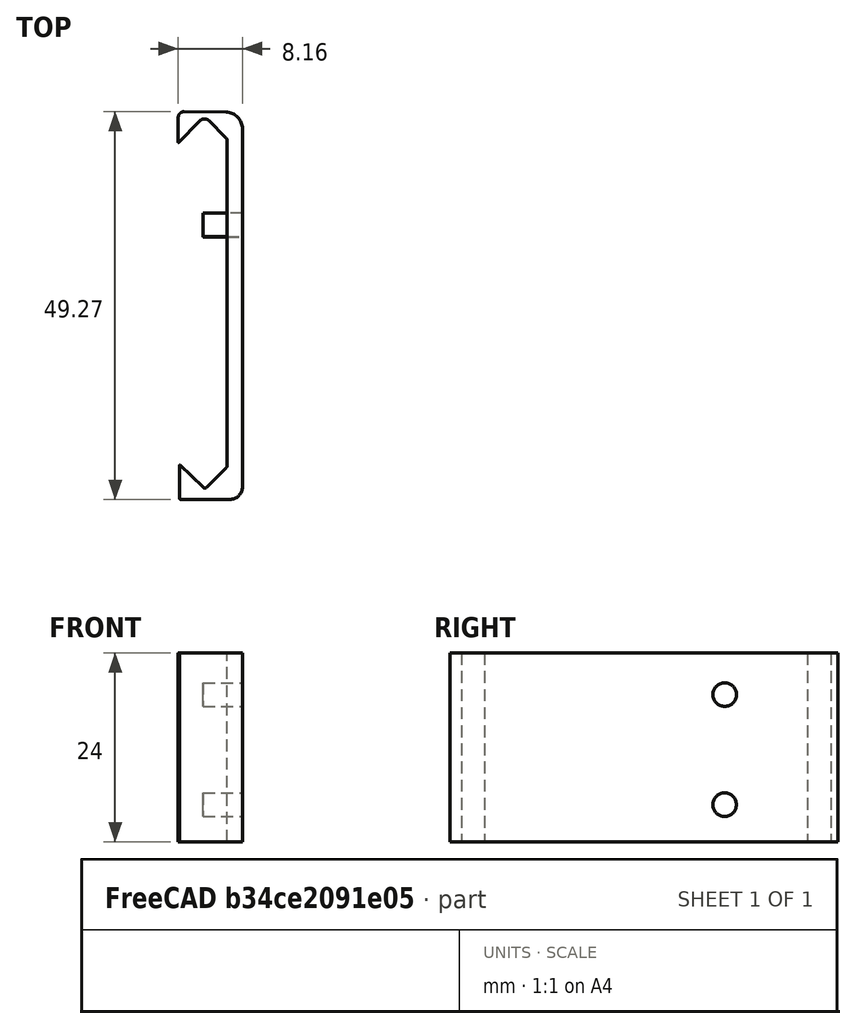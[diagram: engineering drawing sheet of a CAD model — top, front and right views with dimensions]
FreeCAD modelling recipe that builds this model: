
FCSTD DOCUMENT  (FreeCAD 0.14R2935 (Git))
Label: shapeoko-x-axis-limit-switch-mount
License: CC-BY 3.0
LicenseURL: http://creativecommons.org/licenses/by/3.0/
objects: Sketcher::SketchObject×2, PartDesign::Pad×1, PartDesign::Pocket×1
note: 6 computed .brp shape members not serialized (recipe doc carries the construction recipe); baked Part::Feature solids carry a one-line shape summary decoded from their .brp

FEATURE [Sketcher::SketchObject] Sketch002
  sketch-geometry (20):
    g0: LineSegment StartX=10.5567 StartY=23.2356 StartZ=0 EndX=12.6569 EndY=21.1244 EndZ=0
    g1: LineSegment StartX=12.8456 StartY=20.667 StartZ=0 EndX=12.8456 EndY=-20.4936 EndZ=0
    g2: LineSegment StartX=12.691 StartY=-20.8684 StartZ=0 EndX=10.2681 EndY=-23.3051 EndZ=0
    g3: LineSegment StartX=9.74691 StartY=-23.309 StartZ=0 EndX=6.87781 EndY=-20.5076 EndZ=0
    g4: LineSegment StartX=6.77176 StartY=-20.5523 StartZ=0 EndX=6.77176 EndY=-24.6612 EndZ=0
    g5: LineSegment StartX=6.97769 StartY=-24.8671 StartZ=0 EndX=13.1623 EndY=-24.8671 EndZ=0
    g6: LineSegment StartX=14.7796 StartY=-23.2498 StartZ=0 EndX=14.7796 EndY=22.2238 EndZ=0
    g7: LineSegment StartX=12.7053 StartY=24.3261 StartZ=0 EndX=7.38729 EndY=24.3974 EndZ=0
    g8: LineSegment StartX=6.61982 StartY=23.6389 StartZ=0 EndX=6.62491 EndY=20.517 EndZ=0
    g9: ArcOfCircle CenterX=7.37714 CenterY=23.6401 CenterZ=0 NormalX=0 NormalY=0 NormalZ=1 Radius=0.757326 StartAngle=1.5574 EndAngle=3.14322
    g10: ArcOfCircle CenterX=12.6771 CenterY=22.2238 CenterZ=0 NormalX=0 NormalY=0 NormalZ=1 Radius=2.10248 StartAngle=0 EndAngle=1.5574
    g11: ArcOfCircle CenterX=13.1623 CenterY=-23.2498 CenterZ=0 NormalX=0 NormalY=0 NormalZ=1 Radius=1.6173 StartAngle=4.71239 EndAngle=6.28319
    g12: ArcOfCircle CenterX=6.97769 CenterY=-24.6612 CenterZ=0 NormalX=0 NormalY=0 NormalZ=1 Radius=0.205926 StartAngle=3.14159 EndAngle=4.71239
    g13: ArcOfCircle CenterX=6.8342 CenterY=-20.5523 CenterZ=0 NormalX=0 NormalY=0 NormalZ=1 Radius=0.0624343 StartAngle=0.797343 EndAngle=3.14159
    g14: ArcOfCircle CenterX=10.0056 CenterY=-23.044 CenterZ=0 NormalX=0 NormalY=0 NormalZ=1 Radius=0.370259 StartAngle=3.93894 EndAngle=5.50063
    g15: ArcOfCircle CenterX=12.314 CenterY=-20.4936 CenterZ=0 NormalX=0 NormalY=0 NormalZ=1 Radius=0.531611 StartAngle=5.50063 EndAngle=6.28319
    g16: ArcOfCircle CenterX=12.197 CenterY=20.667 CenterZ=0 NormalX=0 NormalY=0 NormalZ=1 Radius=0.648614 StartAngle=0 EndAngle=0.78279
    g17: ArcOfCircle CenterX=9.95822 CenterY=22.6402 CenterZ=0 NormalX=0 NormalY=0 NormalZ=1 Radius=0.844143 StartAngle=0.78279 EndAngle=2.36762
    g18: LineSegment StartX=6.68048 StartY=20.4944 StartZ=0 EndX=9.35454 EndY=23.2303 EndZ=0
    g19: ArcOfCircle CenterX=6.65731 CenterY=20.5171 CenterZ=0 NormalX=0 NormalY=0 NormalZ=1 Radius=0.0323969 StartAngle=3.14322 EndAngle=5.50921
  constraints (25):
    c: Vertical(g1)
    c: Vertical(g4)
    c: Horizontal(g5)
    c: Vertical(g6)
    c: Tangent(g7,g9) = -1.5708
    c: Tangent(g8,g9) = -1.5708
    c: Tangent(g6,g10) = -1.5708
    c: Tangent(g7,g10) = -1.5708
    c: Tangent(g5,g11) = -1.5708
    c: Tangent(g6,g11) = -1.5708
    c: Tangent(g4,g12) = -1.5708
    c: Tangent(g5,g12) = -1.5708
    c: Tangent(g3,g13) = -1.5708
    c: Tangent(g4,g13) = -1.5708
    c: Tangent(g2,g14) = 1.5708
    c: Tangent(g3,g14) = 1.5708
    c: Tangent(g1,g15) = 1.5708
    c: Tangent(g2,g15) = 1.5708
    c: Tangent(g0,g16) = 1.5708
    c: Tangent(g1,g16) = 1.5708
    c: Tangent(g0,g17) = 1.5708
    c: Tangent(g18,g17)
    c: Coincident(g17,g18)
    c: Tangent(g8,g19)
    c: Tangent(g18,g19)
FEATURE [PartDesign::Pad] Pad
  Length = 24
  Length2 = 100
  Sketch = -> Sketch002
  Type = 0
FEATURE [Sketcher::SketchObject] Sketch
  Placement = pos=(14.7796,0,0) rot=(0.57735,0.57735,0.57735;2.0944rad)
  Support = -> Pad [Face13]
  sketch-geometry (2):
    g0: Circle CenterX=9.99647 CenterY=4.72563 CenterZ=0 NormalX=0 NormalY=0 NormalZ=1 Radius=1.5
    g1: Circle CenterX=10.0128 CenterY=18.7154 CenterZ=0 NormalX=0 NormalY=0 NormalZ=1 Radius=1.5
  constraints (2):
    c: Radius(g1) = 1.5
    c: Radius(g0) = 1.5
FEATURE [PartDesign::Pocket] Pocket
  Length = 5
  Sketch = -> Sketch
  Type = 0
